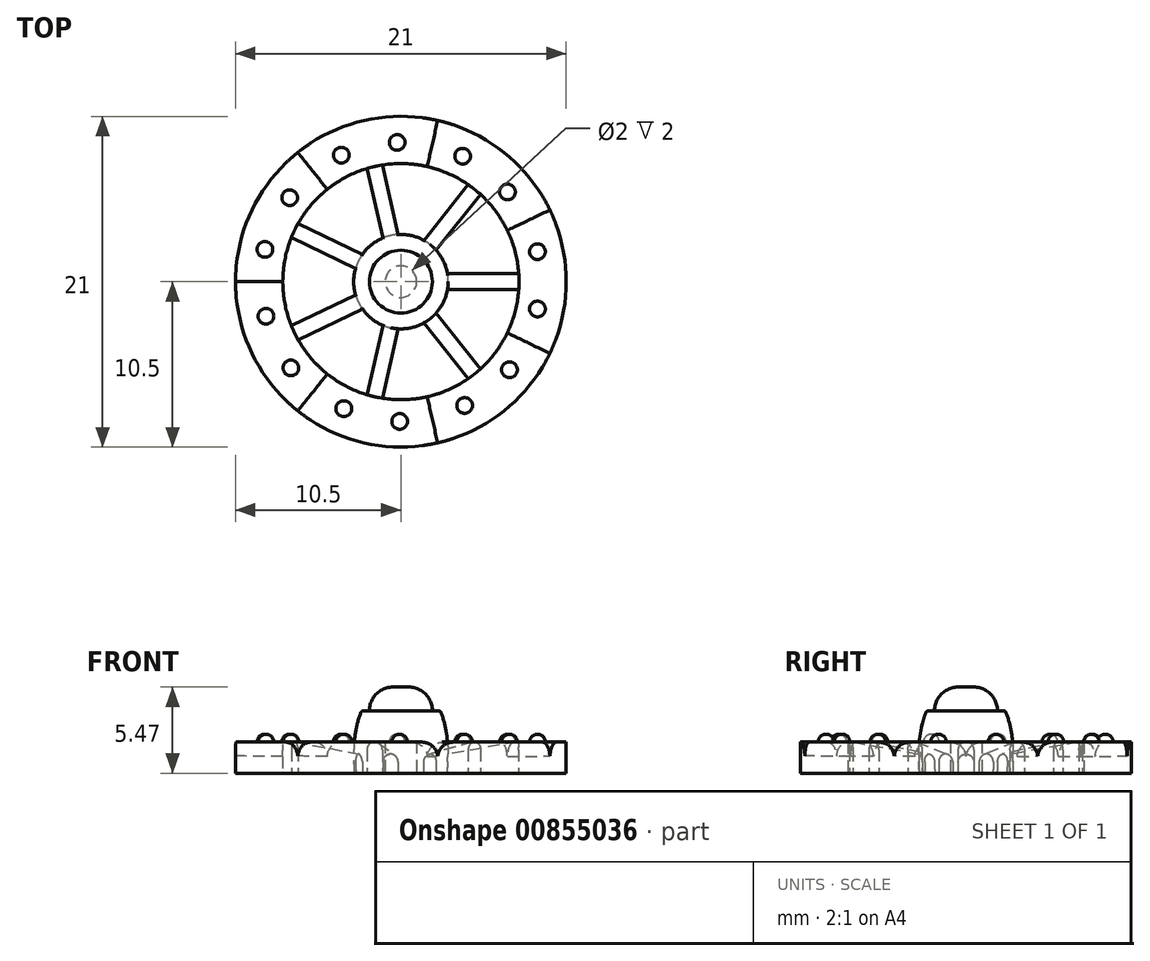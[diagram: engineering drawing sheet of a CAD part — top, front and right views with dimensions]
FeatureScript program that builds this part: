
annotation { "Feature Type Name" : "Feature", "Feature Type Description" : "" }
export const myFeature = defineFeature(function(context is Context, id is Id, definition is map)
    precondition{}
    {
        {
            var Q0;
            Q0=qCreatedBy(makeId("Front.planeOp"),FACE);
            var sketch = newSketch(context, id + "F0", { "sketchPlane" : qUnion([Q0])});
            skLineSegment(sketch, "E0", {"start": v(0, 3) * mm, "end": v(2.5, 3) * mm});
            skLineSegment(sketch, "E1", {"start": v(0, -3) * mm, "end": v(2.5, -3) * mm});
            skFitSpline(sketch, "E2", {"points": [v(2.5, 3) * mm, v(3, 0) * mm, v(2.5, -3) * mm], "startDerivative": vector(2.5, -6) * mm, "endDerivative": vector(-2.5, -6) * mm});
            skLineSegment(sketch, "E3", {"start": v(0, 3) * mm, "end": v(0, -3) * mm});
            skSolve(sketch);
        }
        {
            var Q0;
            Q0=makeQuery(id+"F0.imprint","IMPRINT",FACE,{"disambiguationData":[TD([[makeQuery(id+"F0.imprint","IMPRINT",EDGE,{"derivedFrom":sQuery(id+"F0.wireOp",EDGE,"E0")}),-1.0]])]});
            var Q1;
            Q1=sQuery(id+"F0.wireOp",EDGE,"E3");
            revolve(context, id + "F1", {"surfaceOperationType" : NewSurfaceOperationType.NEW, "entities" : qUnion([Q0]), "axis" : qUnion([Q1]), "revolveType" : RevolveType.SYMMETRIC, "angle" : 51.5 * degree});
        }
        {
            var Q0;
            Q0=qCreatedBy(makeId("Front.planeOp"),FACE);
            var sketch = newSketch(context, id + "F2", { "sketchPlane" : qUnion([Q0])});
            skLineSegment(sketch, "E4", {"start": v(7.5, -0.97) * mm, "end": v(10.5, -0.97) * mm});
            skLineSegment(sketch, "E5", {"start": v(10.5, -0.97) * mm, "end": v(10.5, 1.03) * mm});
            skLineSegment(sketch, "E6", {"start": v(10.5, 1.03) * mm, "end": v(7.5, 1.03) * mm});
            skLineSegment(sketch, "E7", {"start": v(7.5, 1.03) * mm, "end": v(1.59, 0) * mm});
            skPoint(sketch, "E8.0", {"position": v(2.5, -3) * mm});
            skFitSpline(sketch, "E9.0", {"points": [v(2.5, 3) * mm, v(2.92, 2) * mm, v(3.08, 0) * mm, v(2.92, -2) * mm, v(2.5, -3) * mm]});
            skLineSegment(sketch, "E10", {"start": v(7.5, 1.03) * mm, "end": v(7.5, -0.97) * mm});
            skLineSegment(sketch, "E11", {"start": v(1.59, 0) * mm, "end": v(1.59, -0.97) * mm});
            skLineSegment(sketch, "E12", {"start": v(1.59, -0.97) * mm, "end": v(7.5, -0.97) * mm});
            skSolve(sketch);
        }
        {
            var Q0;
            {var subQ0=sQuery(id+"F2.wireOp",EDGE,"E10");Q0=makeQuery(id+"F2.imprint","IMPRINT",FACE,{"disambiguationData":[TD([[makeQuery(id+"F2.imprint","IMPRINT",EDGE,{"derivedFrom":subQ0}),-1.0]])]});}
            var Q1;
            {var subQ0=sQuery(id+"F2.wireOp",EDGE,"E11");Q1=makeQuery(id+"F2.imprint","IMPRINT",FACE,{"disambiguationData":[TD([[makeQuery(id+"F2.imprint","IMPRINT",EDGE,{"derivedFrom":subQ0}),1.0]])]});}
            extrude(context, id + "F3", {"entities" : qUnion([Q0, Q1]), "operationType" : NewBodyOperationType.ADD, "endBound" : BoundingType.SYMMETRIC, "depth" : 1 * mm, "offsetDistance" : 25 * mm});
        }
        {
            var Q0;
            Q0=qCreatedBy(makeId("Top.planeOp"),FACE);
            var sketch = newSketch(context, id + "F4", { "sketchPlane" : qUnion([Q0])});
            skPoint(sketch, "E13.0", {"position": v(7.5, 0) * mm});
            skCircle(sketch, "E14", {"center": v(0, 0) * mm, "radius": 7.5 * mm});
            skCircle(sketch, "E15", {"center": v(0, 0) * mm, "radius": 10.5 * mm});
            skLineSegment(sketch, "E16", {"start": v(0, 0) * mm, "end": v(9.46, 4.56) * mm});
            skLineSegment(sketch, "E17", {"start": v(0, 0) * mm, "end": v(9.46, -4.56) * mm});
            skLineSegment(sketch, "E18", {"start": v(7.5, 0) * mm, "end": v(9.46, 4.56) * mm, "construction": true});
            skLineSegment(sketch, "E19", {"start": v(7.5, 0) * mm, "end": v(9.46, -4.56) * mm, "construction": true});
            skSolve(sketch);
        }
        {
            var Q0;
            {var subQ0=sQuery(id+"F4.wireOp",EDGE,"E16");var subQ1=sQuery(id+"F4.wireOp",EDGE,"E14");var subQ2=makeQuery(id+"F4.imprint","INTERSECT",VERTEX,{"derivedFrom":[subQ1,subQ0]});Q0=makeQuery(id+"F4.imprint","IMPRINT",FACE,{"disambiguationData":[TD([[makeQuery(id+"F4.imprint","IMPRINT",EDGE,{"disambiguationData":[TD([[subQ2,1.0]])],"derivedFrom":subQ1}),-1.0]])]});}
            var Q1;
            Q1=makeQuery(id+"F3.opExtrude","SWEPT_FACE",FACE,{"disambiguationData":[OSD([sQuery(id+"F2.wireOp",EDGE,"E12")])]});
            extrude(context, id + "F5", {"entities" : qUnion([Q0]), "operationType" : NewBodyOperationType.ADD, "depth" : 1 * mm, "offsetDistance" : 25 * mm, "hasSecondDirection" : true, "secondDirectionBound" : SecondDirectionBoundingType.UP_TO_SURFACE, "secondDirectionOppositeDirection" : true, "secondDirectionDepth" : 25 * mm, "secondDirectionBoundEntityFace" : qUnion([Q1])});
        }
        {
            var Q0;
            Q0=makeQuery(id+"F5.opExtrude","CAP_EDGE",EDGE,{"disambiguationData":[OSD([sQuery(id+"F4.wireOp",EDGE,"E17")])],"isStart":false});
            var Q1;
            Q1=makeQuery(id+"F5.opExtrude","CAP_EDGE",EDGE,{"disambiguationData":[OSD([sQuery(id+"F4.wireOp",EDGE,"E16")])],"isStart":false});
            fillet(context, id + "F6", {"entities" : qUnion([Q0, Q1]), "radius" : 1 * mm, "tangentPropagation" : true, "allowEdgeOverflow" : false});
        }
        {
            var Q0;
            Q0=makeQuery(id+"F1.opRevolve","SWEPT_EDGE",EDGE,{"disambiguationData":[OSD([sQuery(id+"F0.wireOp",EDGE,"E0"),sQuery(id+"F0.wireOp",EDGE,"E2")])]});
            var Q1;
            Q1=makeQuery(id+"F1.opRevolve","SWEPT_EDGE",EDGE,{"disambiguationData":[OSD([sQuery(id+"F0.wireOp",EDGE,"E1"),sQuery(id+"F0.wireOp",EDGE,"E2")])]});
            fillet(context, id + "F7", {"entities" : qUnion([Q0, Q1]), "radius" : .2 * mm, "tangentPropagation" : true, "allowEdgeOverflow" : false});
        }
        {
            var Q0;
            Q0=makeQuery(id+"F3.opExtrude","CAP_EDGE",EDGE,{"disambiguationData":[OSD([sQuery(id+"F2.wireOp",EDGE,"E7")])],"isStart":true});
            var Q1;
            Q1=makeQuery(id+"F3.opExtrude","CAP_EDGE",EDGE,{"disambiguationData":[OSD([sQuery(id+"F2.wireOp",EDGE,"E7")])],"isStart":false});
            fillet(context, id + "F8", {"entities" : qUnion([Q0, Q1]), "radius" : .5 * mm, "tangentPropagation" : true, "allowEdgeOverflow" : false});
        }
        {
            var Q0;
            Q0=makeQuery(id+"F5.opExtrude","CAP_FACE",FACE,{"disambiguationData":[OSD([sQuery(id+"F4.wireOp",EDGE,"E14"),sQuery(id+"F4.wireOp",EDGE,"E15"),sQuery(id+"F4.wireOp",EDGE,"E16"),sQuery(id+"F4.wireOp",EDGE,"E17")])],"isStart":false});
            var sketch = newSketch(context, id + "F9", { "sketchPlane" : qUnion([Q0])});
            skLineSegment(sketch, "E20", {"start": v(9.85, -3.64) * mm, "end": v(7.5, 0.16) * mm, "construction": true});
            skLineSegment(sketch, "E21", {"start": v(9.85, 3.64) * mm, "end": v(7.5, 0.16) * mm, "construction": true});
            skCircle(sketch, "E22", {"center": v(8.67, -1.74) * mm, "radius": 0.5 * mm});
            skCircle(sketch, "E23", {"center": v(8.67, 1.9) * mm, "radius": 0.5 * mm});
            skSolve(sketch);
        }
        {
            var Q0;
            Q0=makeQuery(id+"F9.imprint","IMPRINT",FACE,{"disambiguationData":[TD([[makeQuery(id+"F9.imprint","IMPRINT",EDGE,{"derivedFrom":sQuery(id+"F9.wireOp",EDGE,"E22")}),1.0]])]});
            var Q1;
            Q1=makeQuery(id+"F9.imprint","IMPRINT",FACE,{"disambiguationData":[TD([[makeQuery(id+"F9.imprint","IMPRINT",EDGE,{"derivedFrom":sQuery(id+"F9.wireOp",EDGE,"E23")}),1.0]])]});
            extrude(context, id + "F10", {"entities" : qUnion([Q0, Q1]), "operationType" : NewBodyOperationType.ADD, "depth" : 0.5 * mm, "offsetDistance" : 25 * mm});
        }
        {
            var Q0;
            Q0=makeQuery(id+"F10.opExtrude","CAP_EDGE",EDGE,{"disambiguationData":[OSD([sQuery(id+"F9.wireOp",EDGE,"E22")])],"isStart":false});
            var Q1;
            Q1=makeQuery(id+"F10.opExtrude","CAP_EDGE",EDGE,{"disambiguationData":[OSD([sQuery(id+"F9.wireOp",EDGE,"E23")])],"isStart":false});
            fillet(context, id + "F11", {"entities" : qUnion([Q0, Q1]), "radius" : .5 * mm, "tangentPropagation" : true, "allowEdgeOverflow" : false});
        }
        {
            var Q0;
            Q0=makeQuery(id+"F3.opExtrude","SWEPT_BODY",BODY,{"disambiguationData":[OSD([sQuery(id+"F2.wireOp",EDGE,"P3XRHdqQ-L2r8-D6yd-624t-mKVHREpRhMzi"),sQuery(id+"F2.wireOp",EDGE,"E7"),sQuery(id+"F2.wireOp",EDGE,"E9.0"),sQuery(id+"F2.wireOp",EDGE,"E10")])]});
            var Q1;
            Q1=makeQuery(id+"F1.opRevolve","SWEPT_BODY",BODY,{"disambiguationData":[OSD([sQuery(id+"F0.wireOp",EDGE,"E0"),sQuery(id+"F0.wireOp",EDGE,"E1"),sQuery(id+"F0.wireOp",EDGE,"E2"),sQuery(id+"F0.wireOp",EDGE,"E3")])]});
            var Q2;
            Q2=sQuery(id+"F0.wireOp",EDGE,"E3");
            circularPattern(context, id + "F12", {"operationType" : NewBodyOperationType.ADD, "entities" : qUnion([Q0, Q1]), "axis" : qUnion([Q2]), "angle" : 360 * degree, "instanceCount" : 7, "equalSpace" : true});
        }
        {
            var Q0;
            Q0=makeQuery(id+"F1.opRevolve","SWEPT_FACE",FACE,{"disambiguationData":[OSD([sQuery(id+"F0.wireOp",EDGE,"E0")])]});
            var sketch = newSketch(context, id + "F13", { "sketchPlane" : qUnion([Q0])});
            skCircle(sketch, "E24", {"center": v(0, 0) * mm, "radius": 2 * mm});
            skSolve(sketch);
        }
        {
            var Q0;
            Q0=makeQuery(id+"F13.imprint","IMPRINT",FACE,{"disambiguationData":[TD([[makeQuery(id+"F13.imprint","IMPRINT",EDGE,{"derivedFrom":sQuery(id+"F13.wireOp",EDGE,"E24")}),1.0]])]});
            extrude(context, id + "F14", {"entities" : qUnion([Q0]), "operationType" : NewBodyOperationType.ADD, "depth" : 1.5 * mm, "offsetDistance" : 25 * mm});
        }
        {
            var Q0;
            Q0=makeQuery(id+"F14.opExtrude","CAP_EDGE",EDGE,{"disambiguationData":[OSD([sQuery(id+"Fo0OBk3eU98LPMd_1.wireOp",EDGE,"aklb42WT-bPkk-FSHh-G9pr-mXH5jjUrZlTj")])],"isStart":false});
            var Q1;
            Q1=makeQuery(id+"F14.opExtrude","CAP_EDGE",EDGE,{"disambiguationData":[OSD([sQuery(id+"F13.wireOp",EDGE,"E24")])],"isStart":false});
            fillet(context, id + "F15", {"entities" : qUnion([Q0, Q1]), "radius" : 1.5 * mm, "tangentPropagation" : true, "allowEdgeOverflow" : false});
        }
        {
            var Q0;
            Q0=makeQuery(id+"F1.opRevolve","SWEPT_FACE",FACE,{"disambiguationData":[OSD([sQuery(id+"F0.wireOp",EDGE,"E1")])]});
            var sketch = newSketch(context, id + "F16", { "sketchPlane" : qUnion([Q0])});
            skCircle(sketch, "E25", {"center": v(0, 0) * mm, "radius": 1 * mm});
            skSolve(sketch);
        }
        {
            var Q0;
            {var subQ0=makeQuery(id+"F1.opRevolve","SWEPT_FACE",FACE,{"disambiguationData":[OSD([sQuery(id+"F0.wireOp",EDGE,"E1")])]});Q0=makeQuery(id+"F12.boolean.opBoolean","MERGE",FACE,{"derivedFrom":[subQ0,makeQuery(id+"F12.opPattern","COPY",FACE,{"derivedFrom":subQ0,"instanceName":"1"}),makeQuery(id+"F12.opPattern","COPY",FACE,{"derivedFrom":subQ0,"instanceName":"2"}),makeQuery(id+"F12.opPattern","COPY",FACE,{"derivedFrom":subQ0,"instanceName":"3"}),makeQuery(id+"F12.opPattern","COPY",FACE,{"derivedFrom":subQ0,"instanceName":"4"}),makeQuery(id+"F12.opPattern","COPY",FACE,{"derivedFrom":subQ0,"instanceName":"5"}),makeQuery(id+"F12.opPattern","COPY",FACE,{"derivedFrom":subQ0,"instanceName":"6"})]});}
            var sketch = newSketch(context, id + "F17", { "sketchPlane" : qUnion([Q0])});
            skCircle(sketch, "E26", {"center": v(0, 0) * mm, "radius": 3.5 * mm});
            skSolve(sketch);
        }
        {
            var Q0;
            Q0=makeQuery(id+"F17.imprint","IMPRINT",FACE,{"disambiguationData":[TD([[makeQuery(id+"F17.imprint","IMPRINT",EDGE,{"derivedFrom":sQuery(id+"F17.wireOp",EDGE,"E26")}),1.0]])]});
            var Q1;
            Q1=makeQuery(id+"F17.imprint","IMPRINT",FACE,{"disambiguationData":[TD([[makeQuery(id+"F17.imprint","IMPRINT",EDGE,{"derivedFrom":makeQuery(id+"FyldBqjJfOwkMDB_1.boolean.opBoolean","COPY",EDGE,{"derivedFrom":makeQuery(id+"FyldBqjJfOwkMDB_1.opExtrude","CAP_EDGE",EDGE,{"disambiguationData":[OSD([sQuery(id+"F16.wireOp",EDGE,"E25")])],"isStart":true})})}),-1.0]])]});
            var Q2;
            Q2=makeQuery(id+"F16.imprint","IMPRINT",FACE,{"disambiguationData":[TD([[makeQuery(id+"F16.imprint","IMPRINT",EDGE,{"derivedFrom":sQuery(id+"F16.wireOp",EDGE,"E25")}),1.0]])]});
            var Q3;
            Q3=makeQuery(id+"F16.imprint","IMPRINT",FACE,{"disambiguationData":[TD([[makeQuery(id+"F16.imprint","IMPRINT",EDGE,{"derivedFrom":sQuery(id+"F16.wireOp",EDGE,"E25")}),-1.0]])]});
            var Q4;
            {var subQ0=sQuery(id+"F2.wireOp",EDGE,"E12");var subQ1=makeQuery(id+"FhDZsmcsc9Nekxo_1.opExtrude","CAP_FACE",FACE,{"disambiguationData":[OSD([subQ0])],"isStart":false});var subQ2=makeQuery(id+"F5.boolean.opBoolean","MERGE",FACE,{"derivedFrom":[makeQuery(id+"F3.opExtrude","SWEPT_FACE",FACE,{"disambiguationData":[OSD([subQ0])]}),makeQuery(id+"F5.opExtrude","CAP_FACE",FACE,{"disambiguationData":[OSD([subQ0])],"isStart":true})]});Q4=makeQuery(id+"F5OMLmibTjMQsVw_2.boolean.opBoolean","MERGE",FACE,{"derivedFrom":[makeQuery(id+"F12.boolean.opBoolean","MERGE",FACE,{"derivedFrom":[subQ2,makeQuery(id+"F12.opPattern","COPY",FACE,{"derivedFrom":subQ2,"instanceName":"1"}),makeQuery(id+"F12.opPattern","COPY",FACE,{"derivedFrom":subQ2,"instanceName":"2"}),makeQuery(id+"F12.opPattern","COPY",FACE,{"derivedFrom":subQ2,"instanceName":"3"}),makeQuery(id+"F12.opPattern","COPY",FACE,{"derivedFrom":subQ2,"instanceName":"4"}),makeQuery(id+"F12.opPattern","COPY",FACE,{"derivedFrom":subQ2,"instanceName":"5"}),makeQuery(id+"F12.opPattern","COPY",FACE,{"derivedFrom":subQ2,"instanceName":"6"})]}),subQ1,makeQuery(id+"F5OMLmibTjMQsVw_2.opPattern","COPY",FACE,{"derivedFrom":subQ1,"instanceName":"1"}),makeQuery(id+"F5OMLmibTjMQsVw_2.opPattern","COPY",FACE,{"derivedFrom":subQ1,"instanceName":"2"}),makeQuery(id+"F5OMLmibTjMQsVw_2.opPattern","COPY",FACE,{"derivedFrom":subQ1,"instanceName":"3"}),makeQuery(id+"F5OMLmibTjMQsVw_2.opPattern","COPY",FACE,{"derivedFrom":subQ1,"instanceName":"4"}),makeQuery(id+"F5OMLmibTjMQsVw_2.opPattern","COPY",FACE,{"derivedFrom":subQ1,"instanceName":"5"}),makeQuery(id+"F5OMLmibTjMQsVw_2.opPattern","COPY",FACE,{"derivedFrom":subQ1,"instanceName":"6"})]});}
            extrude(context, id + "F18", {"entities" : qUnion([Q0, Q1, Q2, Q3]), "operationType" : NewBodyOperationType.REMOVE, "endBound" : BoundingType.UP_TO_SURFACE, "oppositeDirection" : true, "depth" : 25 * mm, "endBoundEntityFace" : qUnion([Q4]), "offsetDistance" : 25 * mm});
        }
        {
            var Q0;
            {var subQ0=sQuery(id+"F0.wireOp",EDGE,"E2");var subQ1=sQuery(id+"F0.wireOp",EDGE,"E1");var subQ2=sQuery(id+"F2.wireOp",EDGE,"E12");var subQ3=makeQuery(id+"F5.boolean.opBoolean","MERGE",FACE,{"derivedFrom":[makeQuery(id+"F3.opExtrude","SWEPT_FACE",FACE,{"disambiguationData":[OSD([subQ2])]}),makeQuery(id+"F5.opExtrude","CAP_FACE",FACE,{"disambiguationData":[OSD([subQ2])],"isStart":true})]});Q0=makeQuery(id+"F18.boolean.opBoolean","MERGE",FACE,{"derivedFrom":[makeQuery(id+"F12.boolean.opBoolean","MERGE",FACE,{"derivedFrom":[subQ3,makeQuery(id+"F12.opPattern","COPY",FACE,{"derivedFrom":subQ3,"instanceName":"1"}),makeQuery(id+"F12.opPattern","COPY",FACE,{"derivedFrom":subQ3,"instanceName":"2"}),makeQuery(id+"F12.opPattern","COPY",FACE,{"derivedFrom":subQ3,"instanceName":"3"}),makeQuery(id+"F12.opPattern","COPY",FACE,{"derivedFrom":subQ3,"instanceName":"4"}),makeQuery(id+"F12.opPattern","COPY",FACE,{"derivedFrom":subQ3,"instanceName":"5"}),makeQuery(id+"F12.opPattern","COPY",FACE,{"derivedFrom":subQ3,"instanceName":"6"})]})],"fromTools":[makeQuery(id+"F18.opExtrude","CAP_FACE",FACE,{"disambiguationData":[OSD([subQ1,subQ0])],"isStart":false}),makeQuery(id+"F18.opExtrude","CAP_FACE",FACE,{"disambiguationData":[OSD([subQ1,subQ0,sQuery(id+"F17.wireOp",EDGE,"E26")])],"isStart":false})]});}
            var sketch = newSketch(context, id + "F19", { "sketchPlane" : qUnion([Q0])});
            skCircle(sketch, "E27", {"center": v(0, 0) * mm, "radius": 1 * mm});
            skSolve(sketch);
        }
        {
            var Q0;
            Q0=makeQuery(id+"F19.imprint","IMPRINT",FACE,{"disambiguationData":[TD([[makeQuery(id+"F19.imprint","IMPRINT",EDGE,{"derivedFrom":sQuery(id+"F19.wireOp",EDGE,"E27")}),1.0]])]});
            extrude(context, id + "F20", {"entities" : qUnion([Q0]), "operationType" : NewBodyOperationType.REMOVE, "oppositeDirection" : true, "depth" : 2 * mm, "offsetDistance" : 25 * mm});
        }
    });
